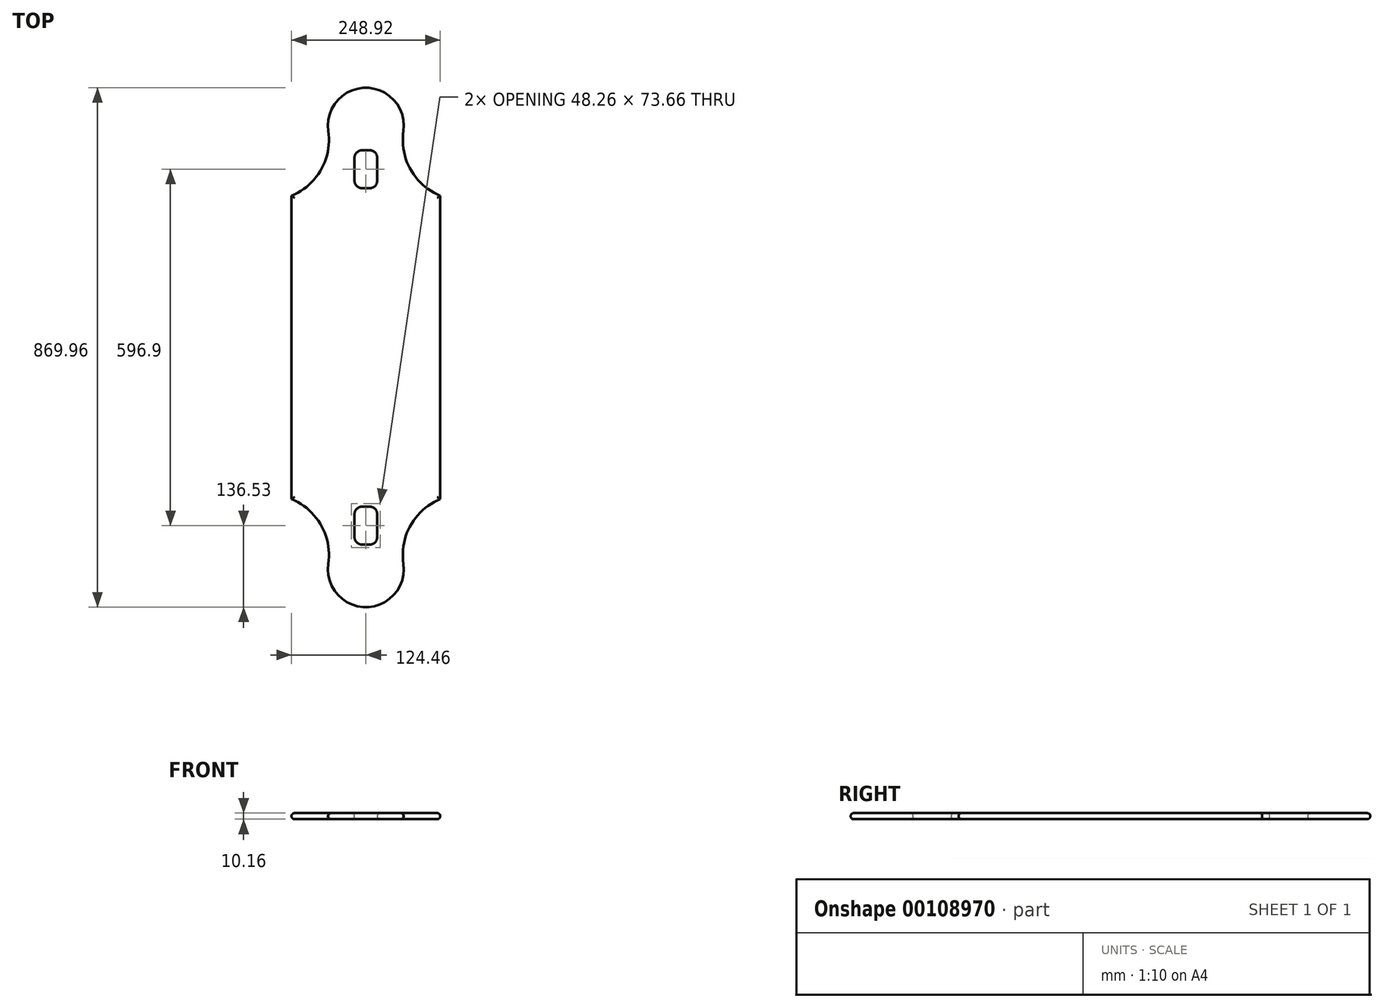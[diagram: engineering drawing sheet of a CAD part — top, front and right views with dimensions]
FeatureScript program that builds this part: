
annotation { "Feature Type Name" : "Feature", "Feature Type Description" : "" }
export const myFeature = defineFeature(function(context is Context, id is Id, definition is map)
    precondition{}
    {
        {
            var Q0;
            Q0=qCreatedBy(makeId("Top.planeOp"),FACE);
            var sketch = newSketch(context, id + "F0", { "sketchPlane" : qUnion([Q0])});
            skLineSegment(sketch, "E0", {"start": v(-124.46, 254) * mm, "end": v(-124.46, -254) * mm});
            skPoint(sketch, "E1", {"position": v(-124.46, 0) * mm});
            skLineSegment(sketch, "E2", {"start": v(0, 434.98) * mm, "end": v(0, -434.98) * mm, "construction": true});
            skPoint(sketch, "E3", {"position": v(0, 0) * mm});
            skArc(sketch, "E4", {"start": v(-62.85, -362.39) * mm, "mid": v(-75.07, -297.63) * mm, "end": v(-124.46, -254) * mm});
            skArc(sketch, "E5", {"start": v(-62.85, -362.39) * mm, "mid": v(-48, -413.04) * mm, "end": v(0, -434.98) * mm});
            skPoint(sketch, "E6.orphan", {"position": v(62.85, -362.39) * mm});
            skLineSegment(sketch, "E7", {"start": v(0, 0) * mm, "end": v(-203.64, 0) * mm, "construction": true});
            skArc(sketch, "E8.MirrorCS", {"start": v(-62.85, 362.39) * mm, "mid": v(-75.07, 297.63) * mm, "end": v(-124.46, 254) * mm});
            skArc(sketch, "E9.MirrorCS", {"start": v(-62.85, 362.39) * mm, "mid": v(-48, 413.04) * mm, "end": v(0, 434.98) * mm});
            skLineSegment(sketch, "E10.MirrorCS", {"start": v(124.46, 254) * mm, "end": v(124.46, -254) * mm});
            skPoint(sketch, "E11.MirrorP", {"position": v(124.46, 0) * mm});
            skArc(sketch, "E12.MirrorCS", {"start": v(62.85, -362.39) * mm, "mid": v(75.07, -297.63) * mm, "end": v(124.46, -254) * mm});
            skArc(sketch, "E13.MirrorCS", {"start": v(62.85, 362.39) * mm, "mid": v(75.07, 297.63) * mm, "end": v(124.46, 254) * mm});
            skArc(sketch, "E14.MirrorCS", {"start": v(62.85, -362.39) * mm, "mid": v(48, -413.04) * mm, "end": v(0, -434.98) * mm});
            skArc(sketch, "E15.MirrorCS", {"start": v(62.85, 362.39) * mm, "mid": v(48, 413.04) * mm, "end": v(0, 434.98) * mm});
            skLineSegment(sketch, "E16", {"start": v(0, 298.45) * mm, "end": v(0, -298.45) * mm});
            skLineSegment(sketch, "E17.bottom", {"start": v(6.35, 330.2) * mm, "end": v(-6.35, 330.2) * mm});
            skLineSegment(sketch, "E17.top", {"start": v(6.35, 266.7) * mm, "end": v(-6.35, 266.7) * mm});
            skLineSegment(sketch, "E17.left", {"start": v(19.05, 317.5) * mm, "end": v(19.05, 279.4) * mm});
            skLineSegment(sketch, "E17.right", {"start": v(-19.05, 317.5) * mm, "end": v(-19.05, 279.4) * mm});
            skPoint(sketch, "E17.middle", {"position": v(0, 298.45) * mm});
            skPoint(sketch, "E18.visualSharp", {"position": v(-19.05, 330.2) * mm});
            skArc(sketch, "E18.filletArc", {"start": v(-6.35, 330.2) * mm, "mid": v(-15.33, 326.48) * mm, "end": v(-19.05, 317.5) * mm});
            skPoint(sketch, "E19.visualSharp", {"position": v(19.05, 330.2) * mm});
            skArc(sketch, "E19.filletArc", {"start": v(19.05, 317.5) * mm, "mid": v(15.33, 326.48) * mm, "end": v(6.35, 330.2) * mm});
            skPoint(sketch, "E20.visualSharp", {"position": v(19.05, 266.7) * mm});
            skArc(sketch, "E20.filletArc", {"start": v(6.35, 266.7) * mm, "mid": v(15.33, 270.42) * mm, "end": v(19.05, 279.4) * mm});
            skPoint(sketch, "E21.visualSharp", {"position": v(-19.05, 266.7) * mm});
            skArc(sketch, "E21.filletArc", {"start": v(-19.05, 279.4) * mm, "mid": v(-15.33, 270.42) * mm, "end": v(-6.35, 266.7) * mm});
            skLineSegment(sketch, "E22.MirrorCS", {"start": v(6.35, -330.2) * mm, "end": v(-6.35, -330.2) * mm});
            skLineSegment(sketch, "E23.MirrorCS", {"start": v(6.35, -266.7) * mm, "end": v(-6.35, -266.7) * mm});
            skArc(sketch, "E24.MirrorCS", {"start": v(19.05, -317.5) * mm, "mid": v(15.33, -326.48) * mm, "end": v(6.35, -330.2) * mm});
            skArc(sketch, "E25.MirrorCS", {"start": v(-19.05, -279.4) * mm, "mid": v(-15.33, -270.42) * mm, "end": v(-6.35, -266.7) * mm});
            skArc(sketch, "E26.MirrorCS", {"start": v(6.35, -266.7) * mm, "mid": v(15.33, -270.42) * mm, "end": v(19.05, -279.4) * mm});
            skArc(sketch, "E27.MirrorCS", {"start": v(-6.35, -330.2) * mm, "mid": v(-15.33, -326.48) * mm, "end": v(-19.05, -317.5) * mm});
            skPoint(sketch, "E28.MirrorP", {"position": v(0, -298.45) * mm});
            skLineSegment(sketch, "E29.MirrorCS", {"start": v(-19.05, -317.5) * mm, "end": v(-19.05, -279.4) * mm});
            skPoint(sketch, "E30.MirrorP", {"position": v(-19.05, -266.7) * mm});
            skPoint(sketch, "E31.MirrorP", {"position": v(19.05, -266.7) * mm});
            skPoint(sketch, "E32.MirrorP", {"position": v(19.05, -330.2) * mm});
            skPoint(sketch, "E33.MirrorP", {"position": v(-19.05, -330.2) * mm});
            skLineSegment(sketch, "E34.MirrorCS", {"start": v(19.05, -317.5) * mm, "end": v(19.05, -279.4) * mm});
            skSolve(sketch);
        }
        {
            var Q0;
            Q0=makeQuery(id+"F0.imprint","IMPRINT",FACE,{"disambiguationData":[TD([[makeQuery(id+"F0.imprint","IMPRINT",EDGE,{"derivedFrom":sQuery(id+"F0.wireOp",EDGE,"E0")}),1.0]])]});
            extrude(context, id + "F1", {"entities" : qUnion([Q0]), "depth" : 10.16 * mm});
        }
        {
            var Q0;
            Q0=makeQuery(id+"F1.opExtrude","CAP_FACE",FACE,{"disambiguationData":[OSD([sQuery(id+"F0.wireOp",EDGE,"E0"),sQuery(id+"F0.wireOp",EDGE,"E4"),sQuery(id+"F0.wireOp",EDGE,"E5"),sQuery(id+"F0.wireOp",EDGE,"E8.MirrorCS"),sQuery(id+"F0.wireOp",EDGE,"E9.MirrorCS"),sQuery(id+"F0.wireOp",EDGE,"E10.MirrorCS"),sQuery(id+"F0.wireOp",EDGE,"E12.MirrorCS"),sQuery(id+"F0.wireOp",EDGE,"E13.MirrorCS"),sQuery(id+"F0.wireOp",EDGE,"E14.MirrorCS"),sQuery(id+"F0.wireOp",EDGE,"E15.MirrorCS"),sQuery(id+"F0.wireOp",EDGE,"E17.bottom"),sQuery(id+"F0.wireOp",EDGE,"E17.top"),sQuery(id+"F0.wireOp",EDGE,"E17.left"),sQuery(id+"F0.wireOp",EDGE,"E17.right"),sQuery(id+"F0.wireOp",EDGE,"E18.filletArc"),sQuery(id+"F0.wireOp",EDGE,"E19.filletArc"),sQuery(id+"F0.wireOp",EDGE,"E20.filletArc"),sQuery(id+"F0.wireOp",EDGE,"E21.filletArc"),sQuery(id+"F0.wireOp",EDGE,"E22.MirrorCS"),sQuery(id+"F0.wireOp",EDGE,"E23.MirrorCS"),sQuery(id+"F0.wireOp",EDGE,"E24.MirrorCS"),sQuery(id+"F0.wireOp",EDGE,"E25.MirrorCS"),sQuery(id+"F0.wireOp",EDGE,"E26.MirrorCS"),sQuery(id+"F0.wireOp",EDGE,"E27.MirrorCS"),sQuery(id+"F0.wireOp",EDGE,"E29.MirrorCS"),sQuery(id+"F0.wireOp",EDGE,"E34.MirrorCS")])],"isStart":false});
            var Q1;
            Q1=makeQuery(id+"F1.opExtrude","CAP_FACE",FACE,{"disambiguationData":[OSD([sQuery(id+"F0.wireOp",EDGE,"E0"),sQuery(id+"F0.wireOp",EDGE,"E4"),sQuery(id+"F0.wireOp",EDGE,"E5"),sQuery(id+"F0.wireOp",EDGE,"E8.MirrorCS"),sQuery(id+"F0.wireOp",EDGE,"E9.MirrorCS"),sQuery(id+"F0.wireOp",EDGE,"E10.MirrorCS"),sQuery(id+"F0.wireOp",EDGE,"E12.MirrorCS"),sQuery(id+"F0.wireOp",EDGE,"E13.MirrorCS"),sQuery(id+"F0.wireOp",EDGE,"E14.MirrorCS"),sQuery(id+"F0.wireOp",EDGE,"E15.MirrorCS"),sQuery(id+"F0.wireOp",EDGE,"E17.bottom"),sQuery(id+"F0.wireOp",EDGE,"E17.top"),sQuery(id+"F0.wireOp",EDGE,"E17.left"),sQuery(id+"F0.wireOp",EDGE,"E17.right"),sQuery(id+"F0.wireOp",EDGE,"E18.filletArc"),sQuery(id+"F0.wireOp",EDGE,"E19.filletArc"),sQuery(id+"F0.wireOp",EDGE,"E20.filletArc"),sQuery(id+"F0.wireOp",EDGE,"E21.filletArc"),sQuery(id+"F0.wireOp",EDGE,"E22.MirrorCS"),sQuery(id+"F0.wireOp",EDGE,"E23.MirrorCS"),sQuery(id+"F0.wireOp",EDGE,"E24.MirrorCS"),sQuery(id+"F0.wireOp",EDGE,"E25.MirrorCS"),sQuery(id+"F0.wireOp",EDGE,"E26.MirrorCS"),sQuery(id+"F0.wireOp",EDGE,"E27.MirrorCS"),sQuery(id+"F0.wireOp",EDGE,"E29.MirrorCS"),sQuery(id+"F0.wireOp",EDGE,"E34.MirrorCS")])],"isStart":true});
            fillet(context, id + "F2", {"entities" : qUnion([Q0, Q1]), "radius" : 5.08 * mm, "tangentPropagation" : true, "allowEdgeOverflow" : false});
        }
    });
